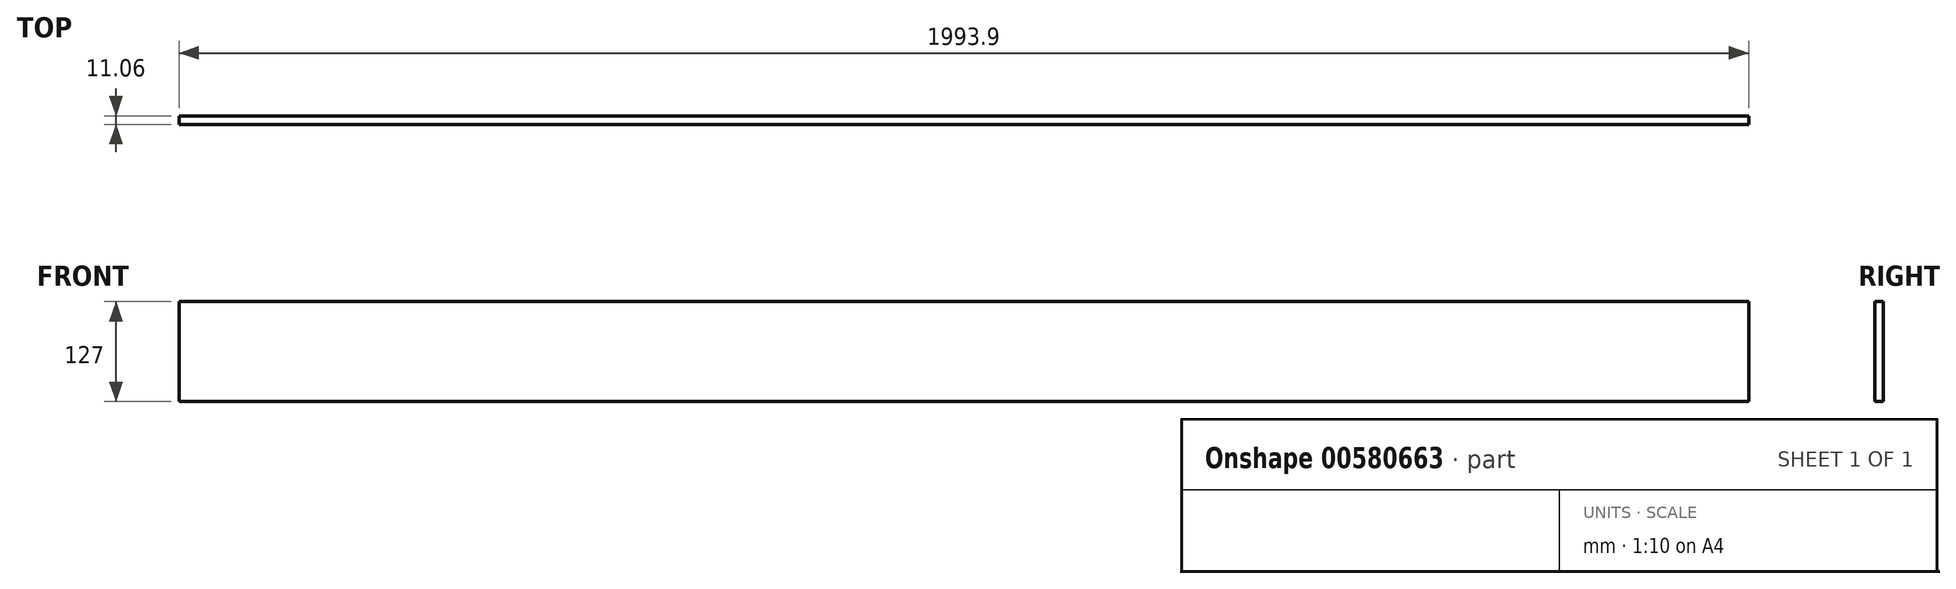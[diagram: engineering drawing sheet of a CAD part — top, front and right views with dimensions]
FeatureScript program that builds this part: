
annotation { "Feature Type Name" : "Feature", "Feature Type Description" : "" }
export const myFeature = defineFeature(function(context is Context, id is Id, definition is map)
    precondition{}
    {
        {
            var Q0;
            Q0=qCreatedBy(makeId("Top.planeOp"),FACE);
            var sketch = newSketch(context, id + "F0", { "sketchPlane" : qUnion([Q0])});
            skLineSegment(sketch, "E0.bottom", {"start": v(-137.5, -5.53) * mm, "end": v(-2131.4, -5.53) * mm});
            skLineSegment(sketch, "E0.top", {"start": v(-137.5, 5.53) * mm, "end": v(-2131.4, 5.53) * mm});
            skPoint(sketch, "E0.middle", {"position": v(0, 0) * mm});
            skPoint(sketch, "E1.orphan", {"position": v(126.45, 5.53) * mm});
            skPoint(sketch, "E0.left.end.orphan", {"position": v(2142.45, 5.53) * mm});
            skLineSegment(sketch, "E2", {"start": v(-2131.4, 5.53) * mm, "end": v(-2131.4, -5.53) * mm});
            skLineSegment(sketch, "E3", {"start": v(-137.5, 5.53) * mm, "end": v(-137.5, -5.53) * mm});
            skSolve(sketch);
        }
        {
            var Q0;
            Q0=makeQuery(id+"F0.imprint","IMPRINT",FACE,{"disambiguationData":[TD([[makeQuery(id+"F0.imprint","IMPRINT",EDGE,{"derivedFrom":sQuery(id+"F0.wireOp",EDGE,"E0.bottom")}),-1.0]])]});
            extrude(context, id + "F1", {"entities" : qUnion([Q0]), "depth" : 127 * mm, "offsetDistance" : 25.4 * mm});
        }
    });
